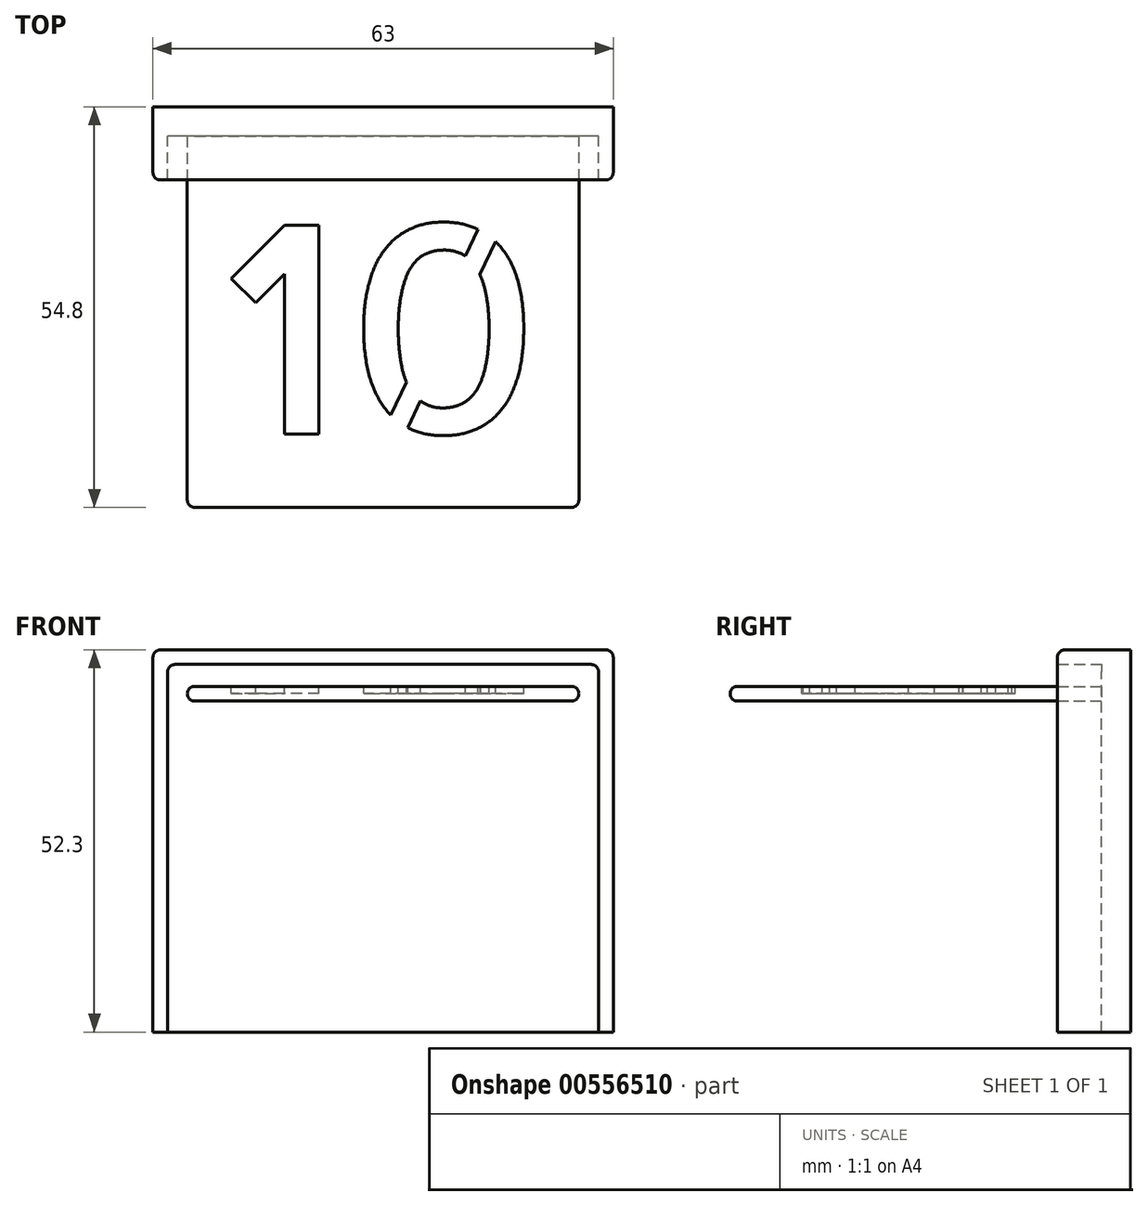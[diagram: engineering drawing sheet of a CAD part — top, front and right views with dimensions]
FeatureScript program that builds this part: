
annotation { "Feature Type Name" : "Feature", "Feature Type Description" : "" }
export const myFeature = defineFeature(function(context is Context, id is Id, definition is map)
    precondition{}
    {
        {
            var Q0;
            Q0=qCreatedBy(makeId("Front.planeOp"),FACE);
            var sketch = newSketch(context, id + "F0", { "sketchPlane" : qUnion([Q0])});
            skLineSegment(sketch, "E0.bottom", {"start": v(29.5, -25.15) * mm, "end": v(-29.5, -25.15) * mm});
            skLineSegment(sketch, "E0.top", {"start": v(29.5, 25.15) * mm, "end": v(-29.5, 25.15) * mm});
            skLineSegment(sketch, "E0.left", {"start": v(29.5, -25.15) * mm, "end": v(29.5, 25.15) * mm});
            skLineSegment(sketch, "E0.right", {"start": v(-29.5, -25.15) * mm, "end": v(-29.5, 25.15) * mm});
            skPoint(sketch, "E0.middle", {"position": v(0, 0) * mm});
            skLineSegment(sketch, "E1.bottom", {"start": v(-26.8, 22.15) * mm, "end": v(26.8, 22.15) * mm});
            skLineSegment(sketch, "E1.top", {"start": v(-26.8, 20.15) * mm, "end": v(26.8, 20.15) * mm});
            skLineSegment(sketch, "E1.left", {"start": v(-26.8, 22.15) * mm, "end": v(-26.8, 20.15) * mm});
            skLineSegment(sketch, "E1.right", {"start": v(26.8, 22.15) * mm, "end": v(26.8, 20.15) * mm});
            skLineSegment(sketch, "E2.bottom", {"start": v(-31.5, -25.15) * mm, "end": v(31.5, -25.15) * mm});
            skLineSegment(sketch, "E2.top", {"start": v(-31.5, 27.15) * mm, "end": v(31.5, 27.15) * mm});
            skLineSegment(sketch, "E2.left", {"start": v(-31.5, -25.15) * mm, "end": v(-31.5, 27.15) * mm});
            skLineSegment(sketch, "E2.right", {"start": v(31.5, -25.15) * mm, "end": v(31.5, 27.15) * mm});
            skSolve(sketch);
        }
        {
            var Q0;
            Q0=makeQuery(id+"F0.imprint","IMPRINT",FACE,{"disambiguationData":[TD([[makeQuery(id+"F0.imprint","IMPRINT",EDGE,{"derivedFrom":sQuery(id+"F0.wireOp",EDGE,"E1.bottom")}),-1.0]])]});
            extrude(context, id + "F1", {"entities" : qUnion([Q0]), "depth" : 54.8 * mm, "offsetDistance" : 25 * mm});
        }
        {
            var Q0;
            Q0=makeQuery(id+"F1.opExtrude","SWEPT_FACE",FACE,{"disambiguationData":[OSD([sQuery(id+"F0.wireOp",EDGE,"E1.bottom")])]});
            var sketch = newSketch(context, id + "F2", { "sketchPlane" : qUnion([Q0])});
            skText(sketch, "E3", { "text": "10", "fontName": "AllertaStencil-Regular.ttf"});
            const initialGuessF2  = {"E3": [-0.0219, -0.0448, 1, 0, 0.02859]};
            skSetInitialGuess(sketch, initialGuessF2);
            skSolve(sketch);
        }
        {
            var Q0;
            Q0 = qSketchRegion(id + "F2", true);
            extrude(context, id + "F3", {"entities" : qUnion([Q0]), "operationType" : NewBodyOperationType.REMOVE, "oppositeDirection" : true, "depth" : 1 * mm, "offsetDistance" : 25 * mm});
        }
        {
            var Q0;
            Q0=makeQuery(id+"F0.imprint","IMPRINT",FACE,{"disambiguationData":[TD([[makeQuery(id+"F0.imprint","IMPRINT",EDGE,{"derivedFrom":sQuery(id+"F0.wireOp",EDGE,"E0.top")}),1.0]])]});
            extrude(context, id + "F4", {"entities" : qUnion([Q0]), "operationType" : NewBodyOperationType.ADD, "depth" : 4 * mm, "offsetDistance" : 25 * mm});
        }
        {
            var Q0;
            Q0=makeQuery(id+"F0.imprint","IMPRINT",FACE,{"disambiguationData":[TD([[makeQuery(id+"F0.imprint","IMPRINT",EDGE,{"derivedFrom":sQuery(id+"F0.wireOp",EDGE,"E0.top")}),-1.0]])]});
            extrude(context, id + "F5", {"entities" : qUnion([Q0]), "operationType" : NewBodyOperationType.ADD, "depth" : 10 * mm, "offsetDistance" : 25 * mm});
        }
        {
            var Q0;
            Q0=makeQuery(id+"F5.opExtrude","SWEPT_EDGE",EDGE,{"disambiguationData":[OSD([sQuery(id+"F0.wireOp",EDGE,"E0.top"),sQuery(id+"F0.wireOp",EDGE,"E0.left")])]});
            var Q1;
            Q1=makeQuery(id+"F5.opExtrude","SWEPT_EDGE",EDGE,{"disambiguationData":[OSD([sQuery(id+"F0.wireOp",EDGE,"E0.top"),sQuery(id+"F0.wireOp",EDGE,"E0.right")])]});
            var Q2;
            Q2=makeQuery(id+"F1.opExtrude","SWEPT_EDGE",EDGE,{"disambiguationData":[OSD([sQuery(id+"F0.wireOp",EDGE,"E1.bottom"),sQuery(id+"F0.wireOp",EDGE,"E1.left")])]});
            var Q3;
            Q3=makeQuery(id+"F1.opExtrude","CAP_EDGE",EDGE,{"disambiguationData":[OSD([sQuery(id+"F0.wireOp",EDGE,"E1.bottom")])],"isStart":false});
            var Q4;
            Q4=makeQuery(id+"F1.opExtrude","CAP_EDGE",EDGE,{"disambiguationData":[OSD([sQuery(id+"F0.wireOp",EDGE,"E1.top")])],"isStart":false});
            var Q5;
            Q5=makeQuery(id+"F1.opExtrude","SWEPT_EDGE",EDGE,{"disambiguationData":[OSD([sQuery(id+"F0.wireOp",EDGE,"E1.top"),sQuery(id+"F0.wireOp",EDGE,"E1.left")])]});
            var Q6;
            Q6=makeQuery(id+"F1.opExtrude","CAP_EDGE",EDGE,{"disambiguationData":[OSD([sQuery(id+"F0.wireOp",EDGE,"E1.left")])],"isStart":false});
            var Q7;
            Q7=makeQuery(id+"F1.opExtrude","SWEPT_EDGE",EDGE,{"disambiguationData":[OSD([sQuery(id+"F0.wireOp",EDGE,"E1.bottom"),sQuery(id+"F0.wireOp",EDGE,"E1.right")])]});
            var Q8;
            Q8=makeQuery(id+"F1.opExtrude","SWEPT_EDGE",EDGE,{"disambiguationData":[OSD([sQuery(id+"F0.wireOp",EDGE,"E1.top"),sQuery(id+"F0.wireOp",EDGE,"E1.right")])]});
            var Q9;
            Q9=makeQuery(id+"F1.opExtrude","CAP_EDGE",EDGE,{"disambiguationData":[OSD([sQuery(id+"F0.wireOp",EDGE,"E1.right")])],"isStart":false});
            var Q10;
            Q10=makeQuery(id+"F5.opExtrude","CAP_EDGE",EDGE,{"disambiguationData":[OSD([sQuery(id+"F0.wireOp",EDGE,"E2.top")])],"isStart":false});
            var Q11;
            Q11=makeQuery(id+"F5.opExtrude","CAP_EDGE",EDGE,{"disambiguationData":[OSD([sQuery(id+"F0.wireOp",EDGE,"E2.left")])],"isStart":false});
            var Q12;
            Q12=makeQuery(id+"F5.opExtrude","SWEPT_EDGE",EDGE,{"disambiguationData":[OSD([sQuery(id+"F0.wireOp",EDGE,"E2.top"),sQuery(id+"F0.wireOp",EDGE,"E2.left")])]});
            var Q13;
            Q13=makeQuery(id+"F5.opExtrude","SWEPT_EDGE",EDGE,{"disambiguationData":[OSD([sQuery(id+"F0.wireOp",EDGE,"E2.top"),sQuery(id+"F0.wireOp",EDGE,"E2.right")])]});
            var Q14;
            Q14=makeQuery(id+"F5.opExtrude","CAP_EDGE",EDGE,{"disambiguationData":[OSD([sQuery(id+"F0.wireOp",EDGE,"E2.right")])],"isStart":false});
            fillet(context, id + "F6", {"entities" : qUnion([Q0, Q1, Q2, Q3, Q4, Q5, Q6, Q7, Q8, Q9, Q10, Q11, Q12, Q13, Q14]), "radius" : 1 * mm, "tangentPropagation" : true, "allowEdgeOverflow" : false});
        }
    });
